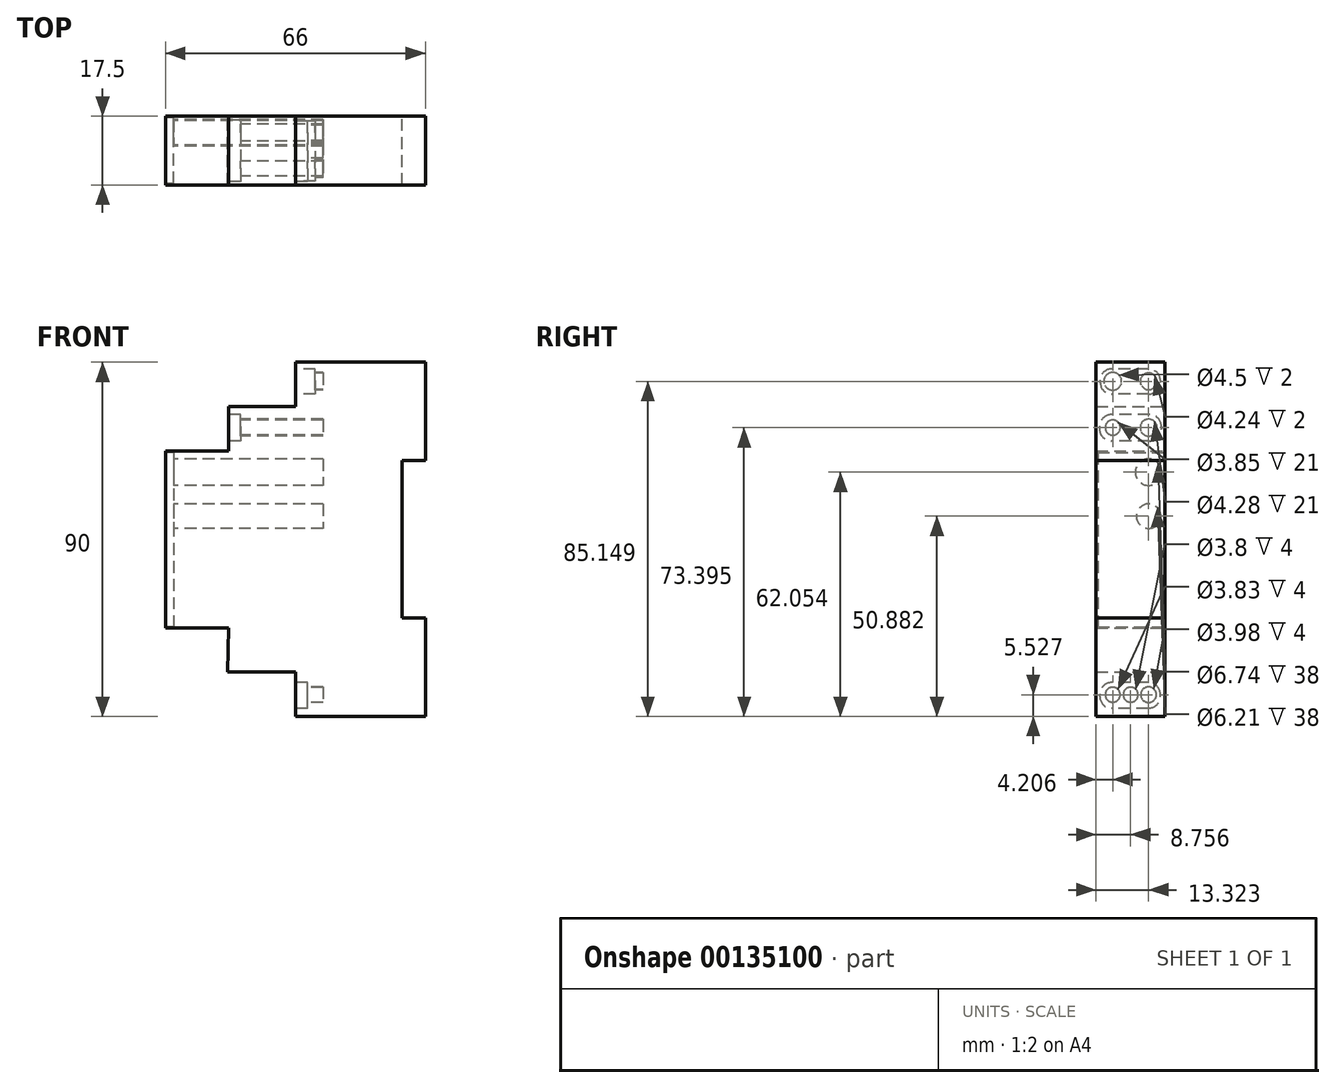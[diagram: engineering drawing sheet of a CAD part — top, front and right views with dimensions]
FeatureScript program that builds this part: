
annotation { "Feature Type Name" : "Feature", "Feature Type Description" : "" }
export const myFeature = defineFeature(function(context is Context, id is Id, definition is map)
    precondition{}
    {
        {
            var Q0;
            Q0=qCreatedBy(makeId("Front.planeOp"),FACE);
            var sketch = newSketch(context, id + "F0", { "sketchPlane" : qUnion([Q0])});
            skLineSegment(sketch, "E0.bottom", {"start": v(-62.04, 123.6) * mm, "end": v(-29.04, 123.6) * mm});
            skLineSegment(sketch, "E0.top", {"start": v(-62.04, 33.6) * mm, "end": v(-29.04, 33.6) * mm});
            skLineSegment(sketch, "E0.left", {"start": v(-95.04, 101.1) * mm, "end": v(-95.04, 56.1) * mm});
            skLineSegment(sketch, "E0.right", {"start": v(-29.04, 123.6) * mm, "end": v(-29.04, 98.6) * mm});
            skLineSegment(sketch, "E1", {"start": v(-62.04, 123.6) * mm, "end": v(-62.04, 112.34) * mm});
            skLineSegment(sketch, "E2", {"start": v(-62.04, 112.34) * mm, "end": v(-79.04, 112.34) * mm});
            skLineSegment(sketch, "E3", {"start": v(-79.04, 112.34) * mm, "end": v(-79.04, 101.1) * mm});
            skLineSegment(sketch, "E4", {"start": v(-79.04, 101.1) * mm, "end": v(-95.04, 101.1) * mm});
            skLineSegment(sketch, "E5", {"start": v(-95.04, 56.1) * mm, "end": v(-79.04, 56.1) * mm});
            skLineSegment(sketch, "E6", {"start": v(-79.04, 56.1) * mm, "end": v(-79.31, 44.84) * mm});
            skLineSegment(sketch, "E7", {"start": v(-79.31, 44.84) * mm, "end": v(-62.04, 44.84) * mm});
            skLineSegment(sketch, "E8", {"start": v(-62.04, 44.84) * mm, "end": v(-62.04, 33.6) * mm});
            skPoint(sketch, "E9.orphan", {"position": v(-95.04, 123.6) * mm});
            skPoint(sketch, "E10.orphan", {"position": v(-95.04, 33.6) * mm});
            skLineSegment(sketch, "E11", {"start": v(-29.04, 98.6) * mm, "end": v(-35.04, 98.6) * mm});
            skLineSegment(sketch, "E12", {"start": v(-35.04, 98.6) * mm, "end": v(-35.04, 58.6) * mm});
            skLineSegment(sketch, "E13", {"start": v(-35.04, 58.6) * mm, "end": v(-29.04, 58.6) * mm});
            skLineSegment(sketch, "E14.trimOffspring", {"start": v(-29.04, 58.6) * mm, "end": v(-29.04, 33.6) * mm});
            skSolve(sketch);
        }
        {
            var Q0;
            Q0=makeQuery(id+"F0.imprint","IMPRINT",FACE,{"disambiguationData":[TD([[makeQuery(id+"F0.imprint","IMPRINT",EDGE,{"derivedFrom":sQuery(id+"F0.wireOp",EDGE,"E0.bottom")}),-1.0]])]});
            extrude(context, id + "F1", {"entities" : qUnion([Q0]), "depth" : 17.5 * mm});
        }
        {
            var Q0;
            Q0=makeQuery(id+"F1.opExtrude","SWEPT_FACE",FACE,{"disambiguationData":[OSD([sQuery(id+"F0.wireOp",EDGE,"E0.left")])]});
            var sketch = newSketch(context, id + "F2", { "sketchPlane" : qUnion([Q0])});
            skCircle(sketch, "E15", {"center": v(4.18, 95.64) * mm, "radius": 3.37 * mm});
            skCircle(sketch, "E16", {"center": v(4.18, 84.47) * mm, "radius": 3.1 * mm});
            skCircle(sketch, "E17", {"center": v(4.18, 106.99) * mm, "radius": 2.14 * mm});
            skCircle(sketch, "E18", {"center": v(13.3, 106.99) * mm, "radius": 1.93 * mm});
            skCircle(sketch, "E19", {"center": v(13.3, 118.74) * mm, "radius": 2.25 * mm});
            skCircle(sketch, "E20", {"center": v(4.18, 118.74) * mm, "radius": 2.12 * mm});
            skCircle(sketch, "E21", {"center": v(4.18, 39.12) * mm, "radius": 1.99 * mm});
            skCircle(sketch, "E22", {"center": v(13.3, 39.12) * mm, "radius": 1.91 * mm});
            skCircle(sketch, "E23", {"center": v(8.74, 39.12) * mm, "radius": 1.9 * mm});
            skSolve(sketch);
        }
        {
            var Q0;
            Q0=makeQuery(id+"F2.imprint","IMPRINT",FACE,{"disambiguationData":[TD([[makeQuery(id+"F2.imprint","IMPRINT",EDGE,{"derivedFrom":sQuery(id+"F2.wireOp",EDGE,"E19")}),1.0]])]});
            var Q1;
            Q1=makeQuery(id+"F2.imprint","IMPRINT",FACE,{"disambiguationData":[TD([[makeQuery(id+"F2.imprint","IMPRINT",EDGE,{"derivedFrom":sQuery(id+"F2.wireOp",EDGE,"E20")}),1.0]])]});
            var Q2;
            Q2=makeQuery(id+"F2.imprint","IMPRINT",FACE,{"disambiguationData":[TD([[makeQuery(id+"F2.imprint","IMPRINT",EDGE,{"derivedFrom":sQuery(id+"F2.wireOp",EDGE,"E17")}),1.0]])]});
            var Q3;
            Q3=makeQuery(id+"F2.imprint","IMPRINT",FACE,{"disambiguationData":[TD([[makeQuery(id+"F2.imprint","IMPRINT",EDGE,{"derivedFrom":sQuery(id+"F2.wireOp",EDGE,"E18")}),1.0]])]});
            var Q4;
            Q4=makeQuery(id+"F2.imprint","IMPRINT",FACE,{"disambiguationData":[TD([[makeQuery(id+"F2.imprint","IMPRINT",EDGE,{"derivedFrom":sQuery(id+"F2.wireOp",EDGE,"E15")}),1.0]])]});
            var Q5;
            Q5=makeQuery(id+"F2.imprint","IMPRINT",FACE,{"disambiguationData":[TD([[makeQuery(id+"F2.imprint","IMPRINT",EDGE,{"derivedFrom":sQuery(id+"F2.wireOp",EDGE,"E16")}),1.0]])]});
            var Q6;
            Q6=makeQuery(id+"F2.imprint","IMPRINT",FACE,{"disambiguationData":[TD([[makeQuery(id+"F2.imprint","IMPRINT",EDGE,{"derivedFrom":sQuery(id+"F2.wireOp",EDGE,"E21")}),1.0]])]});
            var Q7;
            Q7=makeQuery(id+"F2.imprint","IMPRINT",FACE,{"disambiguationData":[TD([[makeQuery(id+"F2.imprint","IMPRINT",EDGE,{"derivedFrom":sQuery(id+"F2.wireOp",EDGE,"E23")}),1.0]])]});
            var Q8;
            Q8=makeQuery(id+"F2.imprint","IMPRINT",FACE,{"disambiguationData":[TD([[makeQuery(id+"F2.imprint","IMPRINT",EDGE,{"derivedFrom":sQuery(id+"F2.wireOp",EDGE,"E22")}),1.0]])]});
            extrude(context, id + "F3", {"entities" : qUnion([Q0, Q1, Q2, Q3, Q4, Q5, Q6, Q7, Q8]), "operationType" : NewBodyOperationType.REMOVE, "oppositeDirection" : true, "depth" : 40 * mm});
        }
        {
            var Q0;
            Q0=makeQuery(id+"F1.opExtrude","SWEPT_FACE",FACE,{"disambiguationData":[OSD([sQuery(id+"F0.wireOp",EDGE,"E1")])]});
            var sketch = newSketch(context, id + "F4", { "sketchPlane" : qUnion([Q0])});
            skLineSegment(sketch, "E24.bottom", {"start": v(4.2, 121.92) * mm, "end": v(13.5, 121.92) * mm});
            skLineSegment(sketch, "E24.top", {"start": v(4.2, 115.51) * mm, "end": v(13.5, 115.51) * mm});
            skLineSegment(sketch, "E24.left", {"start": v(1.2, 118.92) * mm, "end": v(1.2, 118.51) * mm});
            skLineSegment(sketch, "E24.right", {"start": v(16.5, 118.92) * mm, "end": v(16.5, 118.51) * mm});
            skPoint(sketch, "E25.visualSharp", {"position": v(1.2, 121.92) * mm});
            skArc(sketch, "E25.filletArc", {"start": v(4.2, 121.92) * mm, "mid": v(2.09, 121.04) * mm, "end": v(1.2, 118.92) * mm});
            skPoint(sketch, "E26.visualSharp", {"position": v(1.2, 115.51) * mm});
            skArc(sketch, "E26.filletArc", {"start": v(1.2, 118.51) * mm, "mid": v(2.09, 116.39) * mm, "end": v(4.2, 115.51) * mm});
            skPoint(sketch, "E27.visualSharp", {"position": v(16.5, 115.51) * mm});
            skArc(sketch, "E27.filletArc", {"start": v(13.5, 115.51) * mm, "mid": v(15.61, 116.39) * mm, "end": v(16.5, 118.51) * mm});
            skPoint(sketch, "E28.visualSharp", {"position": v(16.5, 121.92) * mm});
            skArc(sketch, "E28.filletArc", {"start": v(16.5, 118.92) * mm, "mid": v(15.61, 121.04) * mm, "end": v(13.5, 121.92) * mm});
            skSolve(sketch);
        }
        {
            var Q0;
            Q0=makeQuery(id+"F4.imprint","IMPRINT",FACE,{"disambiguationData":[TD([[makeQuery(id+"F4.imprint","IMPRINT",EDGE,{"derivedFrom":sQuery(id+"F4.wireOp",EDGE,"E24.bottom")}),-1.0]])]});
            extrude(context, id + "F5", {"entities" : qUnion([Q0]), "operationType" : NewBodyOperationType.REMOVE, "oppositeDirection" : true, "depth" : 5 * mm});
        }
        {
            var Q0;
            Q0=makeQuery(id+"F1.opExtrude","SWEPT_FACE",FACE,{"disambiguationData":[OSD([sQuery(id+"F0.wireOp",EDGE,"E3")])]});
            var sketch = newSketch(context, id + "F6", { "sketchPlane" : qUnion([Q0])});
            skLineSegment(sketch, "E29.bottom", {"start": v(3.93, 110.28) * mm, "end": v(13.66, 110.28) * mm});
            skLineSegment(sketch, "E29.top", {"start": v(3.93, 103.59) * mm, "end": v(13.66, 103.59) * mm});
            skLineSegment(sketch, "E29.left", {"start": v(0.93, 107.28) * mm, "end": v(0.93, 106.59) * mm});
            skLineSegment(sketch, "E29.right", {"start": v(16.66, 107.28) * mm, "end": v(16.66, 106.59) * mm});
            skPoint(sketch, "E30.visualSharp", {"position": v(0.93, 110.28) * mm});
            skArc(sketch, "E30.filletArc", {"start": v(3.93, 110.28) * mm, "mid": v(1.81, 109.4) * mm, "end": v(0.93, 107.28) * mm});
            skPoint(sketch, "E31.visualSharp", {"position": v(0.93, 103.59) * mm});
            skArc(sketch, "E31.filletArc", {"start": v(0.93, 106.59) * mm, "mid": v(1.81, 104.47) * mm, "end": v(3.93, 103.59) * mm});
            skPoint(sketch, "E32.visualSharp", {"position": v(16.66, 103.59) * mm});
            skArc(sketch, "E32.filletArc", {"start": v(13.66, 103.59) * mm, "mid": v(15.78, 104.47) * mm, "end": v(16.66, 106.59) * mm});
            skPoint(sketch, "E33.visualSharp", {"position": v(16.66, 110.28) * mm});
            skArc(sketch, "E33.filletArc", {"start": v(16.66, 107.28) * mm, "mid": v(15.78, 109.4) * mm, "end": v(13.66, 110.28) * mm});
            skSolve(sketch);
        }
        {
            var Q0;
            Q0=makeQuery(id+"F6.imprint","IMPRINT",FACE,{"disambiguationData":[TD([[makeQuery(id+"F6.imprint","IMPRINT",EDGE,{"derivedFrom":sQuery(id+"F6.wireOp",EDGE,"E29.bottom")}),-1.0]])]});
            extrude(context, id + "F7", {"entities" : qUnion([Q0]), "operationType" : NewBodyOperationType.REMOVE, "oppositeDirection" : true, "depth" : 3 * mm});
        }
        {
            var Q0;
            Q0=makeQuery(id+"F1.opExtrude","SWEPT_FACE",FACE,{"disambiguationData":[OSD([sQuery(id+"F0.wireOp",EDGE,"E8")])]});
            var sketch = newSketch(context, id + "F8", { "sketchPlane" : qUnion([Q0])});
            skLineSegment(sketch, "E34.bottom", {"start": v(4.23, 35.68) * mm, "end": v(13.57, 35.68) * mm});
            skLineSegment(sketch, "E34.top", {"start": v(4.23, 42.21) * mm, "end": v(13.57, 42.21) * mm});
            skLineSegment(sketch, "E34.left", {"start": v(1.23, 38.68) * mm, "end": v(1.23, 39.21) * mm});
            skLineSegment(sketch, "E34.right", {"start": v(16.57, 38.68) * mm, "end": v(16.57, 39.21) * mm});
            skPoint(sketch, "E35.visualSharp", {"position": v(16.57, 42.21) * mm});
            skArc(sketch, "E35.filletArc", {"start": v(16.57, 39.21) * mm, "mid": v(15.7, 41.34) * mm, "end": v(13.57, 42.21) * mm});
            skPoint(sketch, "E36.visualSharp", {"position": v(16.57, 35.68) * mm});
            skArc(sketch, "E36.filletArc", {"start": v(13.57, 35.68) * mm, "mid": v(15.7, 36.56) * mm, "end": v(16.57, 38.68) * mm});
            skPoint(sketch, "E37.visualSharp", {"position": v(1.23, 35.68) * mm});
            skArc(sketch, "E37.filletArc", {"start": v(1.23, 38.68) * mm, "mid": v(2.1, 36.56) * mm, "end": v(4.23, 35.68) * mm});
            skPoint(sketch, "E38.visualSharp", {"position": v(1.23, 42.21) * mm});
            skArc(sketch, "E38.filletArc", {"start": v(4.23, 42.21) * mm, "mid": v(2.1, 41.34) * mm, "end": v(1.23, 39.21) * mm});
            skSolve(sketch);
        }
        {
            var Q0;
            Q0=makeQuery(id+"F8.imprint","IMPRINT",FACE,{"disambiguationData":[TD([[makeQuery(id+"F8.imprint","IMPRINT",EDGE,{"derivedFrom":sQuery(id+"F8.wireOp",EDGE,"E34.bottom")}),1.0]])]});
            extrude(context, id + "F9", {"entities" : qUnion([Q0]), "operationType" : NewBodyOperationType.REMOVE, "oppositeDirection" : true, "depth" : 3 * mm});
        }
        {
            var Q0;
            Q0=makeQuery(id+"F1.opExtrude","SWEPT_FACE",FACE,{"disambiguationData":[OSD([sQuery(id+"F0.wireOp",EDGE,"E0.left")])]});
            var sketch = newSketch(context, id + "F10", { "sketchPlane" : qUnion([Q0])});
            skLineSegment(sketch, "E39.bottom", {"start": v(17.09, 100.66) * mm, "end": v(0.28, 100.66) * mm});
            skLineSegment(sketch, "E39.top", {"start": v(17.09, 56.37) * mm, "end": v(0.28, 56.37) * mm});
            skLineSegment(sketch, "E39.left", {"start": v(17.09, 100.66) * mm, "end": v(17.09, 56.37) * mm});
            skLineSegment(sketch, "E39.right", {"start": v(0.28, 100.66) * mm, "end": v(0.28, 56.37) * mm});
            skSolve(sketch);
        }
        {
            var Q0;
            Q0=makeQuery(id+"F10.imprint","IMPRINT",FACE,{"disambiguationData":[TD([[makeQuery(id+"F10.imprint","IMPRINT",EDGE,{"derivedFrom":sQuery(id+"F10.wireOp",EDGE,"E39.bottom")}),1.0]])]});
            extrude(context, id + "F11", {"entities" : qUnion([Q0]), "operationType" : NewBodyOperationType.REMOVE, "oppositeDirection" : true, "depth" : 2 * mm});
        }
    });
